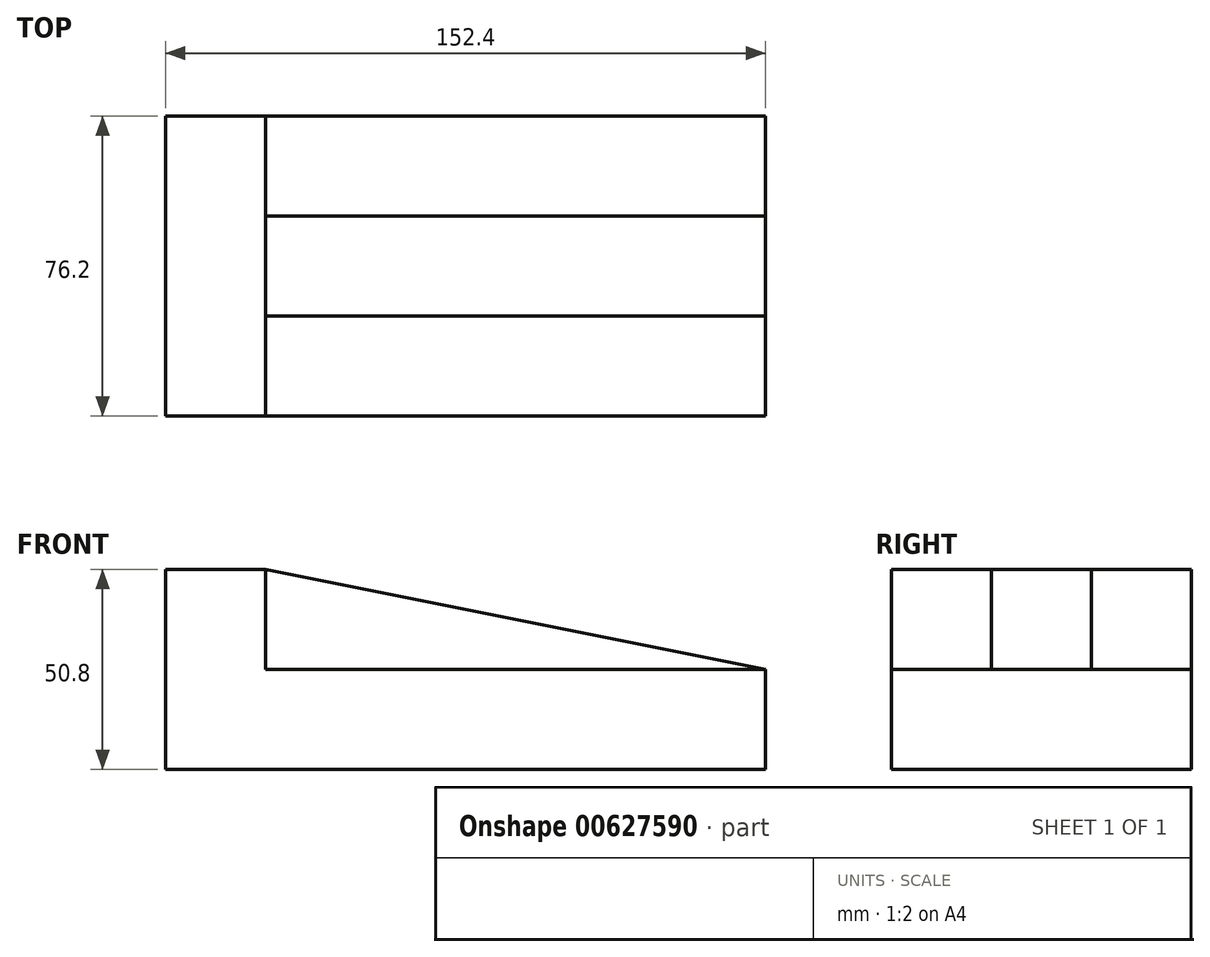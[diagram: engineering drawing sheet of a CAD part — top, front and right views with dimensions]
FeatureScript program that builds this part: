
annotation { "Feature Type Name" : "Feature", "Feature Type Description" : "" }
export const myFeature = defineFeature(function(context is Context, id is Id, definition is map)
    precondition{}
    {
        {
            var Q0;
            Q0=qCreatedBy(makeId("Front.planeOp"),FACE);
            var sketch = newSketch(context, id + "F0", { "sketchPlane" : qUnion([Q0])});
            skLineSegment(sketch, "E0", {"start": v(-31.4, 35.63) * mm, "end": v(-31.4, -15.17) * mm});
            skLineSegment(sketch, "E1", {"start": v(-31.4, -15.17) * mm, "end": v(121, -15.17) * mm});
            skLineSegment(sketch, "E2", {"start": v(121, -15.17) * mm, "end": v(121, 10.23) * mm});
            skLineSegment(sketch, "E3", {"start": v(121, 10.23) * mm, "end": v(-6, 10.23) * mm});
            skLineSegment(sketch, "E4", {"start": v(-6, 10.23) * mm, "end": v(-6, 35.63) * mm});
            skLineSegment(sketch, "E5", {"start": v(-6, 35.63) * mm, "end": v(-31.4, 35.63) * mm});
            skLineSegment(sketch, "E6", {"start": v(-6, 35.63) * mm, "end": v(121, 10.23) * mm});
            skSolve(sketch);
        }
        {
            var Q0;
            Q0=makeQuery(id+"F0.imprint","IMPRINT",FACE,{"disambiguationData":[TD([[makeQuery(id+"F0.imprint","IMPRINT",EDGE,{"derivedFrom":sQuery(id+"F0.wireOp",EDGE,"E0")}),1.0]])]});
            extrude(context, id + "F1", {"entities" : qUnion([Q0]), "oppositeDirection" : true, "depth" : 50.8 * mm, "offsetDistance" : 25.4 * mm});
        }
        {
            var Q0;
            Q0=makeQuery(id+"F0.imprint","IMPRINT",FACE,{"disambiguationData":[TD([[makeQuery(id+"F0.imprint","IMPRINT",EDGE,{"derivedFrom":sQuery(id+"F0.wireOp",EDGE,"E3")}),-1.0]])]});
            extrude(context, id + "F2", {"entities" : qUnion([Q0]), "oppositeDirection" : true, "depth" : 25.4 * mm, "offsetDistance" : 25.4 * mm});
        }
        {
            var Q0;
            Q0=makeQuery(id+"F0.imprint","IMPRINT",FACE,{"disambiguationData":[TD([[makeQuery(id+"F0.imprint","IMPRINT",EDGE,{"derivedFrom":sQuery(id+"F0.wireOp",EDGE,"E0")}),1.0]])]});
            extrude(context, id + "F3", {"entities" : qUnion([Q0]), "operationType" : NewBodyOperationType.ADD, "depth" : 25.4 * mm, "offsetDistance" : 25.4 * mm});
        }
    });
